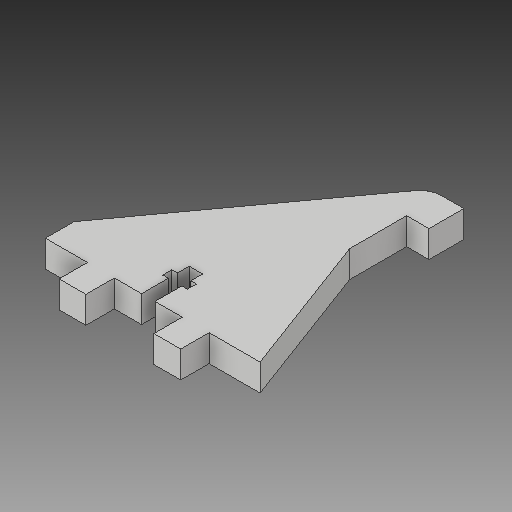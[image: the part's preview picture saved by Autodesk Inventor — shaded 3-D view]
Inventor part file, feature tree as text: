
AUTODESK INVENTOR PART (.ipt)
format: ipt  version: 2018 (Build 220112000, 112)  size: 120,832 bytes
history: native  units: mm
features: extrude x1, sketch x1
ambient origin geometry x8: Origin, YZ Plane, XZ Plane, XY Plane, X Axis, Y Axis, Z Axis, Center Point
bodies: Solid1 (feature_tree)
feature tree (2):
  extrude  "Extrusion1"  [1 undecoded]
  sketch  "Sketch1"  dims[d0=6.0mm d1=0.0mm]
note: 1 required parameter value undecoded (feature->parameter linkage not recoverable at this tier; creation-order binding heuristic only, values carry confidence <= 0.55)
